# Revit family: URA_Eclairage_de_Securite_URALIFE V_NOIR_LSC – pose Plafond
name_source: partatom
category: Luminaires
units: mm (PartAtom-declared; Revit-internal decimal feet)

## family parameters
Cote de connecteur circulaire = Utiliser le diamètre
Couper avec des vides une fois chargée = Non
Hôte = Face
Numéro OmniClass = 23.80.70.11.21
Partagée = Non
Repere pour localisation dans la piece = Non
Source d'éclairage = Non
Titre OmniClass = Emergency Lighting
Type d'élément = Normal

## types (4) — shared parameters
Alimentation de secours = Centralisé (source centrale)
Classe de protection = II
Conditions Générale d'Utilisation = https://export.legrand.com
Couleur = Noir
Elévation par défaut = 2300 mm
Entraxe de fixation horizontale = 184-188
Fabricant = URA
Fréquence = 50-60
Hauteur encastrement = 55 mm  [stored 0.180446 ft]
IK = 07
IP = 43
Largeur = 62 mm  [stored 0.203412 ft]
Largeur encastrement = 70 mm  [stored 0.229659 ft]
Longueur = 219 mm
Longueur d'encastrement = 245 mm  [stored 0.803806 ft]
Matière = Plastique
Mode de pose = En saillie et encastré
Objet Connecté = Oui
Système de contrôle = sans
Temperature d'utilisation MIN-MAX = 0-35
Tension = 48-230 AC/DC
Type de commutation = Non permanent
Type de connexion = autre
URL = www.ura.fr
capacité des bornes = 1.5
source lumineuse = LED non interchangeable
zero-valued in all types: Entraxe de fixation verticale

## per-type parameters (varying)
| type | Consommation en veille | Désignation produit | Flux lumineux utile | Fonction | Hauteur | Percement | Picto AMB | Picto EVAC | Puissance du système | Référence / Modèle | Type de pictogramme | Visibilité AMB Encastré | Visibilité AMB Saillie | Visibilité EVAC Encastré | Visibilité EVAC Saillie |
| .4-LSC Ambiance 48-230V pose plafond en saillie (noir) | 22.0 mA | LSC URALIFE V NOIR, AMBIANCE, 48-220VDC / 230VAC, POSE PLAFOND ENCASTREE OU SAILLIE | 400 lm | Éclairage d'ambiance (anti-panique) | 36 mm  [stored 0.11811 ft] | 250 mm  [stored 0.82021 ft] | Oui | Non | 5 W | UR-128424V |  | Non | Oui | Non | Non |
| .3-LSC Ambiance 48-230V pose plafond encastrée (noir) | 22.0 mA | LSC URALIFE V NOIR, AMBIANCE, 48-220VDC / 230VAC, POSE PLAFOND ENCASTREE OU SAILLIE | 400 lm | Éclairage d'ambiance (anti-panique) | 36 mm  [stored 0.11811 ft] | -55 mm  [stored -0.180446 ft] | Oui | Non | 5 W | UR-128424V |  | Oui | Non | Non | Non |
| .2-LSC Evacuation 48-230V pose plafond en saillie (noir) | 6.5 mA | LSC URALIFE V NOIR, EVACUATION, 48-220VDC / 230VAC, POSE PLAFOND ENCASTREE OU SAILLIE | 45 lm | Éclairage d'évacuation | 138 mm | 250 mm  [stored 0.82021 ft] | Non | Oui | 2 W | UR-128414V | Feuillet/plaque inséré(e) | Non | Non | Non | Oui |
| .1-LSC Evacuation 48-230V pose plafond encastrée (noir) | 6.5 mA | LSC URALIFE V NOIR, EVACUATION, 48-220VDC / 230VAC, POSE PLAFOND ENCASTREE OU SAILLIE | 45 lm | Éclairage d'évacuation | 138 mm | -55 mm  [stored -0.180446 ft] | Non | Oui | 2 W | UR-128414V | Feuillet/plaque inséré(e) | Non | Non | Oui | Non |

note: [stored X ft] marks values corroborated as IEEE doubles in the binary element streams (Revit-internal decimal feet)
